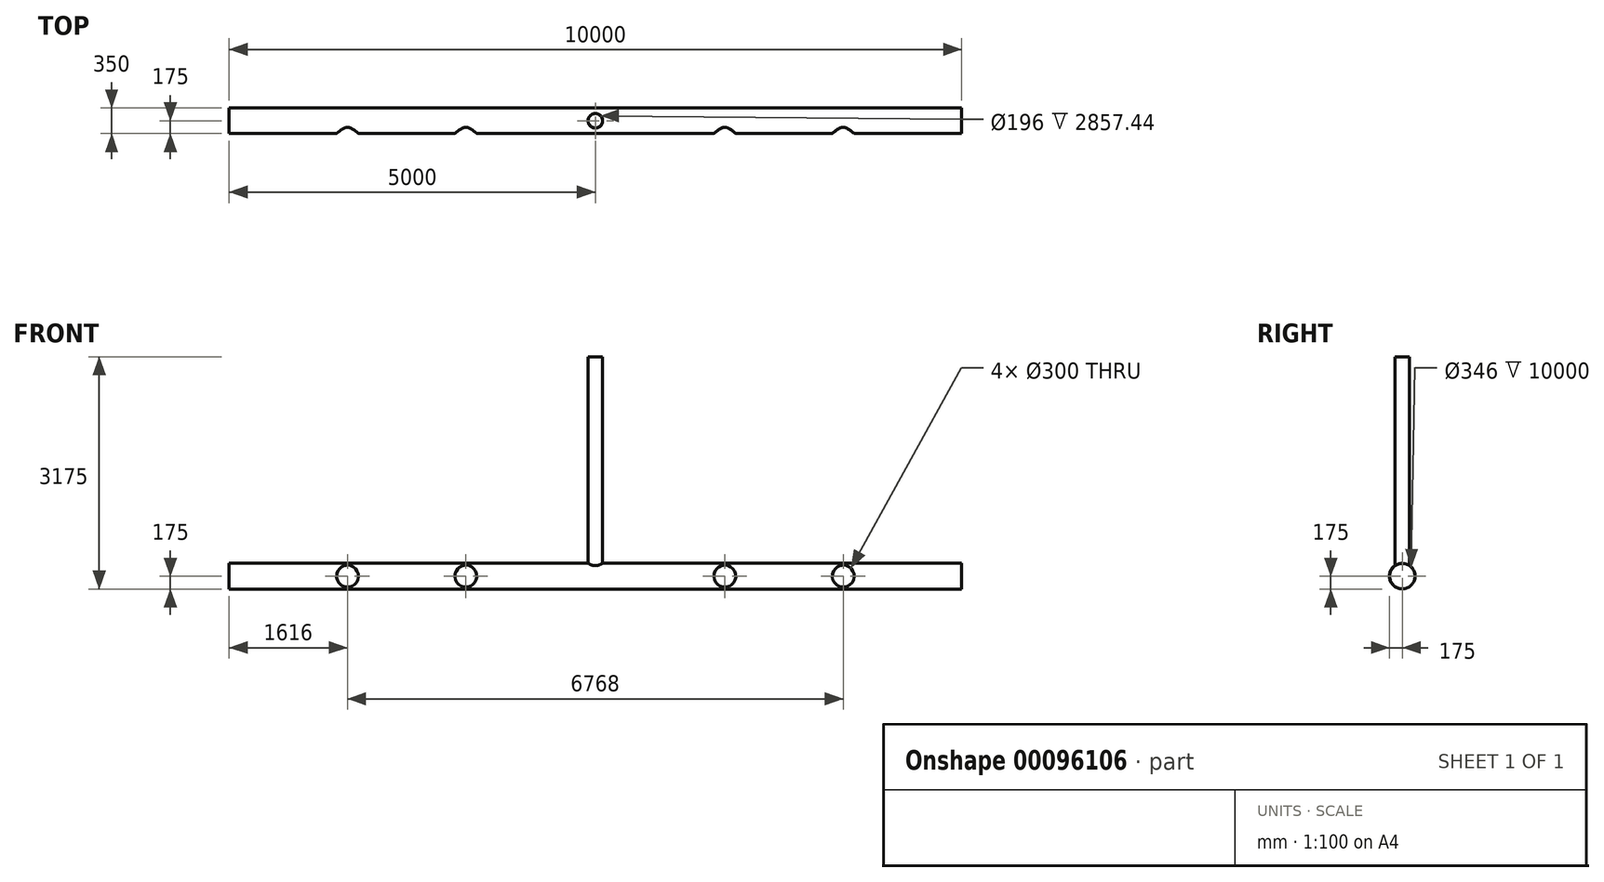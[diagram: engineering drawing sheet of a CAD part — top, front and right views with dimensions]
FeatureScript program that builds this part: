
annotation { "Feature Type Name" : "Feature", "Feature Type Description" : "" }
export const myFeature = defineFeature(function(context is Context, id is Id, definition is map)
    precondition{}
    {
        {
            var Q0;
            Q0=qCreatedBy(makeId("Top.planeOp"),FACE);
            var sketch = newSketch(context, id + "F0", { "sketchPlane" : qUnion([Q0])});
            skCircle(sketch, "E0", {"center": v(0, 0) * mm, "radius": 98 * mm});
            skCircle(sketch, "E1", {"center": v(0, 0) * mm, "radius": 100 * mm});
            skSolve(sketch);
        }
        {
            var Q0;
            Q0=qCreatedBy(makeId("Front.planeOp"),FACE);
            var sketch = newSketch(context, id + "F1", { "sketchPlane" : qUnion([Q0])});
            skLineSegment(sketch, "E2", {"start": v(0, 0) * mm, "end": v(0, -3000) * mm});
            skLineSegment(sketch, "E3", {"start": v(-5000, -3000) * mm, "end": v(5000, -3000) * mm});
            skCircle(sketch, "E4", {"center": v(-3384, -3000) * mm, "radius": 150 * mm});
            skCircle(sketch, "E5", {"center": v(-1768, -3000) * mm, "radius": 150 * mm});
            skCircle(sketch, "E6", {"center": v(1768, -3000) * mm, "radius": 150 * mm});
            skCircle(sketch, "E7", {"center": v(3384, -3000) * mm, "radius": 150 * mm});
            skSolve(sketch);
        }
        {
            var Q0;
            Q0=qCreatedBy(makeId("Right.planeOp"),FACE);
            var sketch = newSketch(context, id + "F2", { "sketchPlane" : qUnion([Q0])});
            skCircle(sketch, "E8", {"center": v(0, -3000) * mm, "radius": 0.06 * mm});
            skCircle(sketch, "E9", {"center": v(0, -3000) * mm, "radius": 175 * mm});
            skCircle(sketch, "E10", {"center": v(0, -3000) * mm, "radius": 173 * mm});
            skSolve(sketch);
        }
        {
            var Q0;
            Q0=makeQuery(id+"F2.imprint","IMPRINT",FACE,{"disambiguationData":[TD([[makeQuery(id+"F2.imprint","IMPRINT",EDGE,{"derivedFrom":sQuery(id+"F2.wireOp",EDGE,"E9")}),1.0]])]});
            extrude(context, id + "F3", {"entities" : qUnion([Q0]), "endBound" : BoundingType.SYMMETRIC, "depth" : 10000 * mm});
        }
        {
            var Q0;
            Q0=makeQuery(id+"F0.imprint","IMPRINT",FACE,{"disambiguationData":[TD([[makeQuery(id+"F0.imprint","IMPRINT",EDGE,{"derivedFrom":sQuery(id+"F0.wireOp",EDGE,"E0")}),1.0]])]});
            var Q1;
            Q1=sQuery(id+"F1.wireOp",EDGE,"E2");
            sweep(context, id + "F4", {"operationType" : NewBodyOperationType.REMOVE, "profiles" : qUnion([Q0]), "path" : qUnion([Q1])});
        }
        {
            var Q0;
            Q0=sQuery(id+"F1.wireOp",VERTEX,"E4.center");
            var Q1;
            Q1=sQuery(id+"F1.wireOp",VERTEX,"E5.center");
            var Q2;
            Q2=sQuery(id+"F1.wireOp",VERTEX,"E6.center");
            var Q3;
            Q3=sQuery(id+"F1.wireOp",VERTEX,"E7.center");
            var Q4;
            Q4=makeQuery(id+"F3.opExtrude","SWEPT_BODY",BODY,{"disambiguationData":[OSD([sQuery(id+"F2.wireOp",EDGE,"E9"),sQuery(id+"F2.wireOp",EDGE,"E10")])]});
            hole(context, id + "F5", {"style" : HoleStyle.SIMPLE, "endStyle" : HoleEndStyle.THROUGH, "oppositeDirection" : true, "holeDiameter" : 300 * mm, "locations" : qUnion([Q0, Q1, Q2, Q3]), "scope" : qUnion([Q4]), "isTappedThrough" : true});
        }
        {
            var Q0;
            Q0=makeQuery(id+"F0.imprint","IMPRINT",FACE,{"disambiguationData":[TD([[makeQuery(id+"F0.imprint","IMPRINT",EDGE,{"derivedFrom":sQuery(id+"F0.wireOp",EDGE,"E0")}),-1.0]])]});
            var Q1;
            Q1=makeQuery(id+"F3.opExtrude","SWEPT_FACE",FACE,{"disambiguationData":[OSD([sQuery(id+"F2.wireOp",EDGE,"E9")])]});
            extrude(context, id + "F6", {"entities" : qUnion([Q0]), "operationType" : NewBodyOperationType.ADD, "endBound" : BoundingType.UP_TO_SURFACE, "oppositeDirection" : true, "endBoundEntityFace" : qUnion([Q1]), "depth" : 25 * mm});
        }
    });
